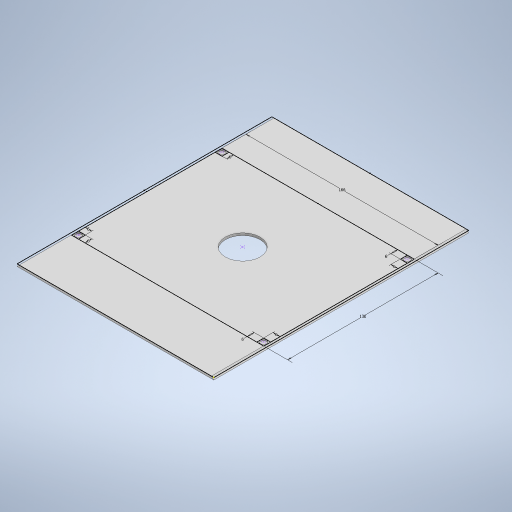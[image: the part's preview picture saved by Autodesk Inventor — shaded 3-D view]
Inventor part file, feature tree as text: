
AUTODESK INVENTOR PART (.ipt)
format: ipt  version: 2024 (Build 280153020, 153B)  size: 245,248 bytes
history: native  units: mm
features: hole x3, extrude x1, chamfer x1, sketch x1
ambient origin geometry x8: Origin, YZ Plane, XZ Plane, XY Plane, X Axis, Y Axis, Z Axis, Center Point
bodies: Solid1 (feature_tree)
feature tree (6):
  extrude  "base"  Depth=220.0mm
  chamfer  "chamfers"  Distance=2.0mm
  hole  "holes"  [1 undecoded]
  hole  "magnet_holders"  [1 undecoded]
  hole  "wire_hole"  [1 undecoded]
  sketch  "Sketch1"  dims[d0=170.0mm d1=220.0mm d2=2.0mm d3=0.0mm d7=2.0mm d8=2.0mm d9=45.0deg d10=166.0mm d11=130.0mm d12=6.0mm d13=6.0mm d14=6.0mm d15=6.0mm d16=6.0mm d17=6.0mm d18=6.0mm d19=5.5mm d20=6.0mm d21=4.0mm d22=2.0mm d23=90.0deg d24=1.0mm d25=0.0mm d26=30.0mm d27=6.0mm d28=4.0mm d29=2.0mm d30=90.0deg d31=1.0mm d32=0.0mm]
note: 3 required parameter values undecoded (feature->parameter linkage not recoverable at this tier; creation-order binding heuristic only, values carry confidence <= 0.55)
